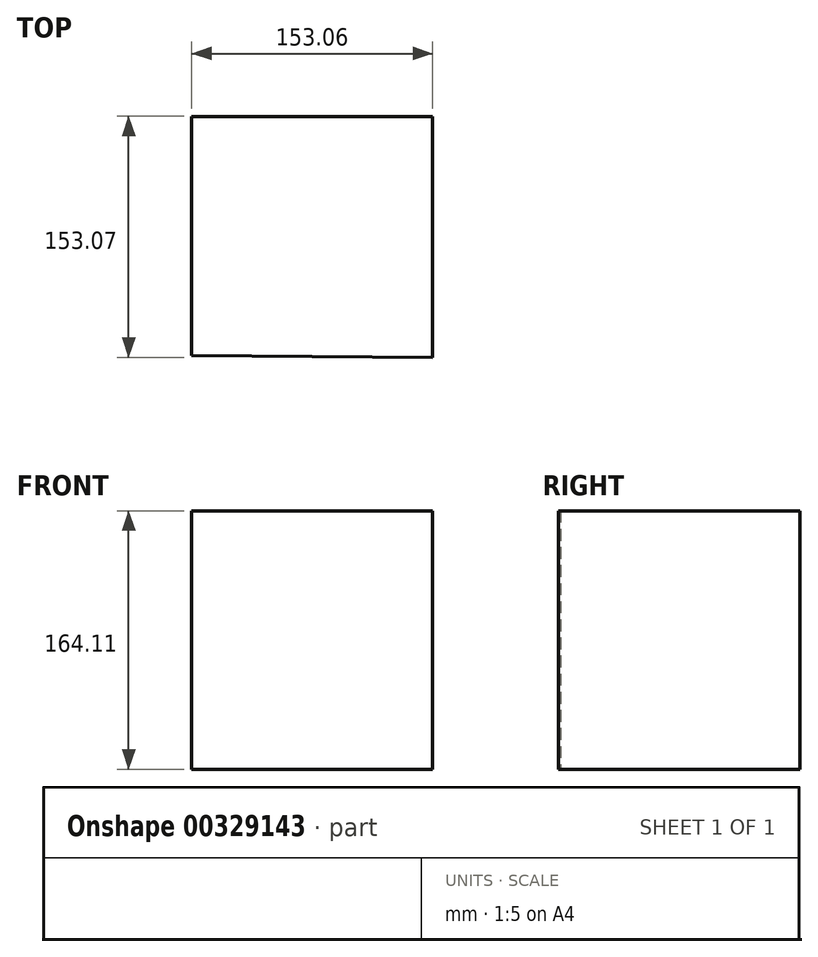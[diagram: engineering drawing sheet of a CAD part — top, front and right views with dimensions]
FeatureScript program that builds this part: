
annotation { "Feature Type Name" : "Feature", "Feature Type Description" : "" }
export const myFeature = defineFeature(function(context is Context, id is Id, definition is map)
    precondition{}
    {
        {
            var Q0;
            Q0=qCreatedBy(makeId("Top.planeOp"),FACE);
            var sketch = newSketch(context, id + "F0", { "sketchPlane" : qUnion([Q0])});
            skLineSegment(sketch, "E0", {"start": v(-76.53, -75.99) * mm, "end": v(-76.53, 75.99) * mm});
            skLineSegment(sketch, "E1", {"start": v(-76.53, 75.99) * mm, "end": v(76.53, 75.99) * mm});
            skLineSegment(sketch, "E2", {"start": v(76.53, 75.99) * mm, "end": v(76.53, -77.08) * mm});
            skLineSegment(sketch, "E3", {"start": v(76.53, -77.08) * mm, "end": v(-76.53, -75.99) * mm});
            skSolve(sketch);
        }
        {
            var Q0;
            Q0 = qSketchRegion(id + "F0", true);
            extrude(context, id + "F1", {"entities" : qUnion([Q0]), "depth" : 25.4 * mm});
        }
        {
            var Q0;
            Q0=makeQuery(id+"F1.opExtrude","CAP_FACE",FACE,{"disambiguationData":[OSD([sQuery(id+"F0.wireOp",EDGE,"E0"),sQuery(id+"F0.wireOp",EDGE,"E1"),sQuery(id+"F0.wireOp",EDGE,"E2"),sQuery(id+"F0.wireOp",EDGE,"E3")])],"isStart":false});
            extrude(context, id + "F2", {"entities" : qUnion([Q0]), "operationType" : NewBodyOperationType.ADD, "depth" : 50.63 * mm});
        }
        {
            var Q0;
            Q0=makeQuery(id+"F1.opExtrude","CAP_FACE",FACE,{"disambiguationData":[OSD([sQuery(id+"F0.wireOp",EDGE,"E0"),sQuery(id+"F0.wireOp",EDGE,"E1"),sQuery(id+"F0.wireOp",EDGE,"E2"),sQuery(id+"F0.wireOp",EDGE,"E3")])],"isStart":true});
            extrude(context, id + "F3", {"entities" : qUnion([Q0]), "operationType" : NewBodyOperationType.ADD, "depth" : 88.08 * mm});
        }
    });
